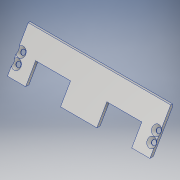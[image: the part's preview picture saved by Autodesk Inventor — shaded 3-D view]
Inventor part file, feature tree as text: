
AUTODESK INVENTOR PART (.ipt)
format: ipt  version: 2019 (Build 230136000, 136)  size: 145,920 bytes
history: native  units: mm
features: sketch x3, extrude x2, other x1, hole x1
ambient origin geometry x8: Origin, YZ Plane, XZ Plane, XY Plane, X Axis, Y Axis, Z Axis, Center Point
bodies: Body1 (feature_tree)
feature tree (7):
  other  "Bryła1"
  extrude  "Wyciągnięcie proste1"  TaperAngle=60.0deg  [1 undecoded]
  extrude  "Wyciągnięcie proste2"  Depth=2.0mm
  hole  "Otwór1"  [1 undecoded]
  sketch  "Szkic1"
  sketch  "Szkic2"
  sketch  "Szkic3"
note: 2 required parameter values undecoded (feature->parameter linkage not recoverable at this tier; creation-order binding heuristic only, values carry confidence <= 0.55)
